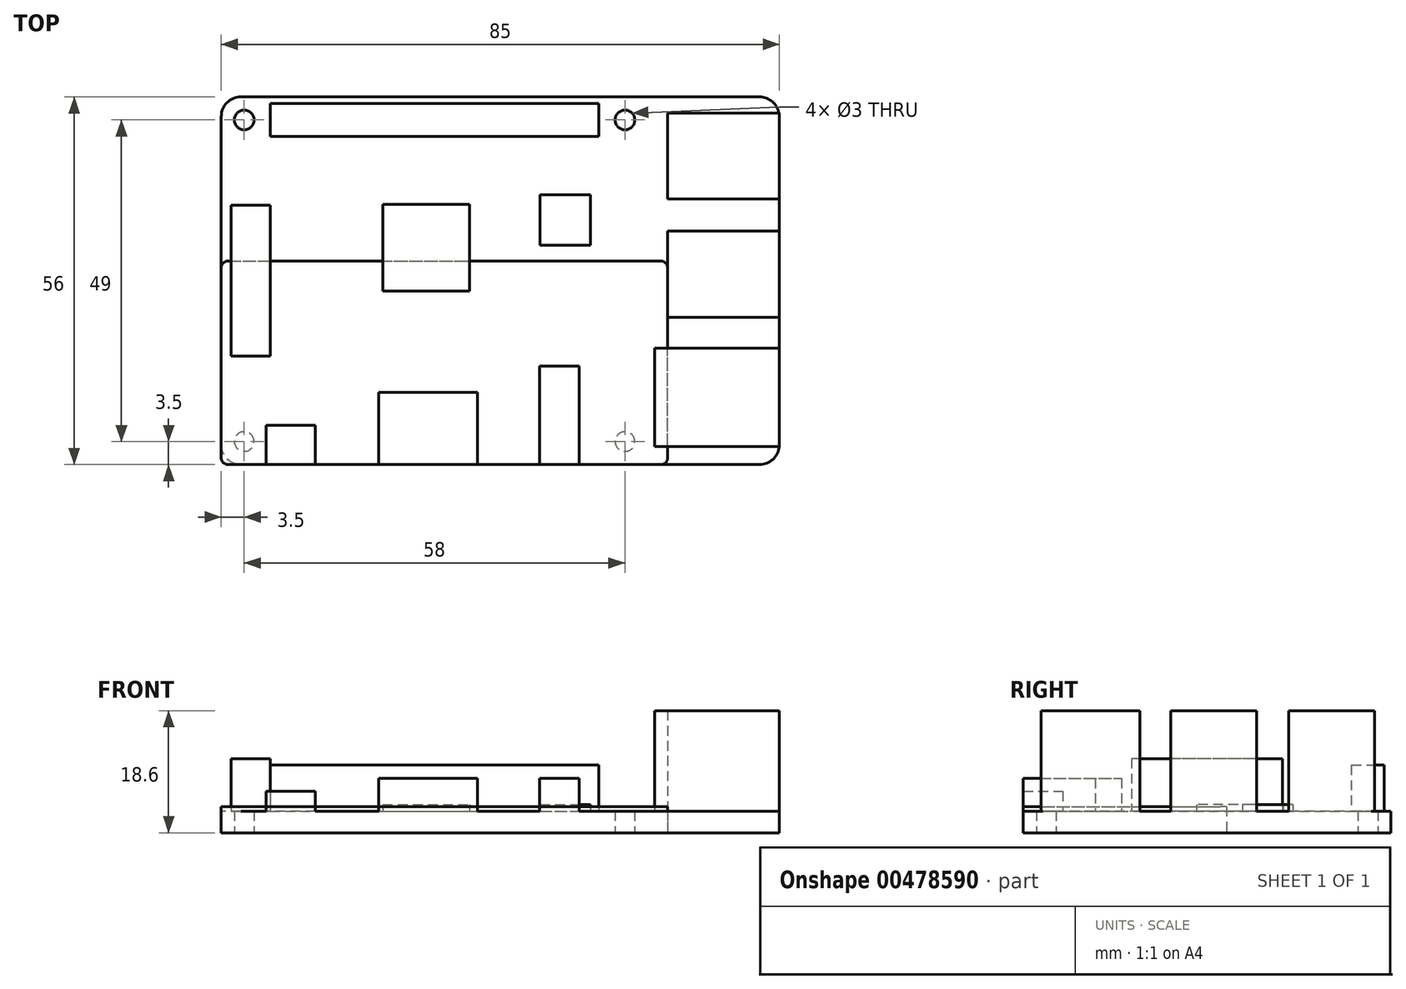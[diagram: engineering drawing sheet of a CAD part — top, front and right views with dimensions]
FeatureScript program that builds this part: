
annotation { "Feature Type Name" : "Feature", "Feature Type Description" : "" }
export const myFeature = defineFeature(function(context is Context, id is Id, definition is map)
    precondition{}
    {
        {
            var Q0;
            Q0=qCreatedBy(makeId("Top.planeOp"),FACE);
            var sketch = newSketch(context, id + "F0", { "sketchPlane" : qUnion([Q0])});
            skLineSegment(sketch, "E0.bottom", {"start": v(0, 0) * mm, "end": v(85, 0) * mm});
            skLineSegment(sketch, "E0.top", {"start": v(0, 56) * mm, "end": v(85, 56) * mm});
            skLineSegment(sketch, "E0.left", {"start": v(0, 0) * mm, "end": v(0, 56) * mm});
            skLineSegment(sketch, "E0.right", {"start": v(85, 0) * mm, "end": v(85, 56) * mm});
            skCircle(sketch, "E1", {"center": v(3.5, 52.5) * mm, "radius": 1.5 * mm});
            skLineSegment(sketch, "E2", {"start": v(0, 28) * mm, "end": v(85, 28) * mm, "construction": true});
            skLineSegment(sketch, "E3", {"start": v(32.5, 56) * mm, "end": v(32.5, 0) * mm, "construction": true});
            skCircle(sketch, "E4.MirrorC", {"center": v(3.5, 3.5) * mm, "radius": 1.5 * mm});
            skCircle(sketch, "E5.MirrorC", {"center": v(61.5, 3.5) * mm, "radius": 1.5 * mm});
            skCircle(sketch, "E6.MirrorC", {"center": v(61.5, 52.5) * mm, "radius": 1.5 * mm});
            skSolve(sketch);
        }
        {
            var Q0;
            Q0=makeQuery(id+"F0.imprint","IMPRINT",FACE,{"disambiguationData":[TD([[makeQuery(id+"F0.imprint","IMPRINT",EDGE,{"derivedFrom":sQuery(id+"F0.wireOp",EDGE,"E0.bottom")}),1.0]])]});
            extrude(context, id + "F1", {"entities" : qUnion([Q0]), "depth" : 3.3 * mm});
        }
        {
            var Q0;
            Q0=makeQuery(id+"F1.opExtrude","SWEPT_EDGE",EDGE,{"disambiguationData":[OSD([sQuery(id+"F0.wireOp",EDGE,"E0.top"),sQuery(id+"F0.wireOp",EDGE,"E0.left")])]});
            var Q1;
            Q1=makeQuery(id+"F1.opExtrude","SWEPT_EDGE",EDGE,{"disambiguationData":[OSD([sQuery(id+"F0.wireOp",EDGE,"E0.top"),sQuery(id+"F0.wireOp",EDGE,"E0.right")])]});
            var Q2;
            Q2=makeQuery(id+"F1.opExtrude","SWEPT_EDGE",EDGE,{"disambiguationData":[OSD([sQuery(id+"F0.wireOp",EDGE,"E0.bottom"),sQuery(id+"F0.wireOp",EDGE,"E0.left")])]});
            var Q3;
            Q3=makeQuery(id+"F1.opExtrude","SWEPT_EDGE",EDGE,{"disambiguationData":[OSD([sQuery(id+"F0.wireOp",EDGE,"E0.bottom"),sQuery(id+"F0.wireOp",EDGE,"E0.right")])]});
            fillet(context, id + "F2", {"entities" : qUnion([Q0, Q1, Q2, Q3]), "radius" : 3 * mm, "tangentPropagation" : true, "allowEdgeOverflow" : false});
        }
        {
            var Q0;
            Q0=makeQuery(id+"F1.opExtrude","CAP_FACE",FACE,{"disambiguationData":[OSD([sQuery(id+"F0.wireOp",EDGE,"E0.bottom"),sQuery(id+"F0.wireOp",EDGE,"E0.top"),sQuery(id+"F0.wireOp",EDGE,"E0.left"),sQuery(id+"F0.wireOp",EDGE,"E0.right"),sQuery(id+"F0.wireOp",EDGE,"E1"),sQuery(id+"F0.wireOp",EDGE,"E4.MirrorC"),sQuery(id+"F0.wireOp",EDGE,"E5.MirrorC"),sQuery(id+"F0.wireOp",EDGE,"E6.MirrorC")])],"isStart":false});
            var sketch = newSketch(context, id + "F3", { "sketchPlane" : qUnion([Q0])});
            skLineSegment(sketch, "E7.bottom", {"start": v(7.5, 50) * mm, "end": v(57.5, 50) * mm});
            skLineSegment(sketch, "E7.top", {"start": v(7.5, 55) * mm, "end": v(57.5, 55) * mm});
            skLineSegment(sketch, "E7.left", {"start": v(7.5, 50) * mm, "end": v(7.5, 55) * mm});
            skLineSegment(sketch, "E7.right", {"start": v(57.5, 50) * mm, "end": v(57.5, 55) * mm});
            skCircle(sketch, "E8.0", {"center": v(3.5, 52.5) * mm, "radius": 1.5 * mm, "construction": true});
            skLineSegment(sketch, "E9", {"start": v(32.5, 55) * mm, "end": v(32.5, 50) * mm, "construction": true});
            skLineSegment(sketch, "E10", {"start": v(3.5, 52.5) * mm, "end": v(32.5, 52.5) * mm, "construction": true});
            skSolve(sketch);
        }
        {
            var Q0;
            Q0 = qSketchRegion(id + "F3", true);
            extrude(context, id + "F4", {"entities" : qUnion([Q0]), "operationType" : NewBodyOperationType.ADD, "depth" : 7 * mm});
        }
        {
            var Q0;
            Q0=makeQuery(id+"F1.opExtrude","CAP_FACE",FACE,{"disambiguationData":[OSD([sQuery(id+"F0.wireOp",EDGE,"E0.bottom"),sQuery(id+"F0.wireOp",EDGE,"E0.top"),sQuery(id+"F0.wireOp",EDGE,"E0.left"),sQuery(id+"F0.wireOp",EDGE,"E0.right"),sQuery(id+"F0.wireOp",EDGE,"E1"),sQuery(id+"F0.wireOp",EDGE,"E4.MirrorC"),sQuery(id+"F0.wireOp",EDGE,"E5.MirrorC"),sQuery(id+"F0.wireOp",EDGE,"E6.MirrorC")])],"isStart":false});
            var sketch = newSketch(context, id + "F5", { "sketchPlane" : qUnion([Q0])});
            skLineSegment(sketch, "E11.bottom", {"start": v(1.5, 39.5) * mm, "end": v(7.5, 39.5) * mm});
            skLineSegment(sketch, "E11.top", {"start": v(1.5, 16.5) * mm, "end": v(7.5, 16.5) * mm});
            skLineSegment(sketch, "E11.left", {"start": v(1.5, 39.5) * mm, "end": v(1.5, 16.5) * mm});
            skLineSegment(sketch, "E11.right", {"start": v(7.5, 39.5) * mm, "end": v(7.5, 16.5) * mm});
            skCircle(sketch, "E12.0", {"center": v(3.5, 52.5) * mm, "radius": 1.5 * mm, "construction": true});
            skCircle(sketch, "E13.0", {"center": v(3.5, 3.5) * mm, "radius": 1.5 * mm, "construction": true});
            skLineSegment(sketch, "E14", {"start": v(3.5, 3.5) * mm, "end": v(3.5, 52.5) * mm, "construction": true});
            skLineSegment(sketch, "E15", {"start": v(3.5, 28) * mm, "end": v(7.5, 28) * mm, "construction": true});
            skSolve(sketch);
        }
        {
            var Q0;
            Q0 = qSketchRegion(id + "F5", true);
            extrude(context, id + "F6", {"entities" : qUnion([Q0]), "operationType" : NewBodyOperationType.ADD, "depth" : 8 * mm});
        }
        {
            var Q0;
            Q0=makeQuery(id+"F1.opExtrude","CAP_FACE",FACE,{"disambiguationData":[OSD([sQuery(id+"F0.wireOp",EDGE,"E0.bottom"),sQuery(id+"F0.wireOp",EDGE,"E0.top"),sQuery(id+"F0.wireOp",EDGE,"E0.left"),sQuery(id+"F0.wireOp",EDGE,"E0.right"),sQuery(id+"F0.wireOp",EDGE,"E1"),sQuery(id+"F0.wireOp",EDGE,"E4.MirrorC"),sQuery(id+"F0.wireOp",EDGE,"E5.MirrorC"),sQuery(id+"F0.wireOp",EDGE,"E6.MirrorC")])],"isStart":false});
            var sketch = newSketch(context, id + "F7", { "sketchPlane" : qUnion([Q0])});
            skLineSegment(sketch, "E16.bottom", {"start": v(68, 53.55) * mm, "end": v(85, 53.55) * mm});
            skLineSegment(sketch, "E16.top", {"start": v(68, 40.45) * mm, "end": v(85, 40.45) * mm});
            skLineSegment(sketch, "E16.left", {"start": v(68, 53.55) * mm, "end": v(68, 40.45) * mm});
            skLineSegment(sketch, "E16.right", {"start": v(85, 53.55) * mm, "end": v(85, 40.45) * mm});
            skLineSegment(sketch, "E17.bottom", {"start": v(68, 35.55) * mm, "end": v(85, 35.55) * mm});
            skLineSegment(sketch, "E17.top", {"start": v(68, 22.45) * mm, "end": v(85, 22.45) * mm});
            skLineSegment(sketch, "E17.left", {"start": v(68, 35.55) * mm, "end": v(68, 22.45) * mm});
            skLineSegment(sketch, "E17.right", {"start": v(85, 35.55) * mm, "end": v(85, 22.45) * mm});
            skLineSegment(sketch, "E18.bottom", {"start": v(66, 17.75) * mm, "end": v(85, 17.75) * mm});
            skLineSegment(sketch, "E18.top", {"start": v(66, 2.75) * mm, "end": v(85, 2.75) * mm});
            skLineSegment(sketch, "E18.left", {"start": v(66, 17.75) * mm, "end": v(66, 2.75) * mm});
            skLineSegment(sketch, "E18.right", {"start": v(85, 17.75) * mm, "end": v(85, 2.75) * mm});
            skLineSegment(sketch, "E19", {"start": v(68, 29) * mm, "end": v(85, 29) * mm, "construction": true});
            skLineSegment(sketch, "E20", {"start": v(68, 47) * mm, "end": v(85, 47) * mm, "construction": true});
            skLineSegment(sketch, "E21", {"start": v(66, 10.25) * mm, "end": v(85, 10.25) * mm, "construction": true});
            skSolve(sketch);
        }
        {
            var Q0;
            Q0 = qSketchRegion(id + "F7", true);
            extrude(context, id + "F8", {"entities" : qUnion([Q0]), "operationType" : NewBodyOperationType.ADD, "depth" : 15.3 * mm});
        }
        {
            var Q0;
            Q0=makeQuery(id+"F1.opExtrude","CAP_FACE",FACE,{"disambiguationData":[OSD([sQuery(id+"F0.wireOp",EDGE,"E0.bottom"),sQuery(id+"F0.wireOp",EDGE,"E0.top"),sQuery(id+"F0.wireOp",EDGE,"E0.left"),sQuery(id+"F0.wireOp",EDGE,"E0.right"),sQuery(id+"F0.wireOp",EDGE,"E1"),sQuery(id+"F0.wireOp",EDGE,"E4.MirrorC"),sQuery(id+"F0.wireOp",EDGE,"E5.MirrorC"),sQuery(id+"F0.wireOp",EDGE,"E6.MirrorC")])],"isStart":false});
            var sketch = newSketch(context, id + "F9", { "sketchPlane" : qUnion([Q0])});
            skLineSegment(sketch, "E22.bottom", {"start": v(24, 0) * mm, "end": v(39, 0) * mm});
            skLineSegment(sketch, "E22.top", {"start": v(24, 11) * mm, "end": v(39, 11) * mm});
            skLineSegment(sketch, "E22.left", {"start": v(24, 0) * mm, "end": v(24, 11) * mm});
            skLineSegment(sketch, "E22.right", {"start": v(39, 0) * mm, "end": v(39, 11) * mm});
            skLineSegment(sketch, "E23", {"start": v(31.5, 11) * mm, "end": v(31.5, 0) * mm, "construction": true});
            skSolve(sketch);
        }
        {
            var Q0;
            Q0 = qSketchRegion(id + "F9", true);
            extrude(context, id + "F10", {"entities" : qUnion([Q0]), "operationType" : NewBodyOperationType.ADD, "depth" : 5 * mm});
        }
        {
            var Q0;
            Q0=makeQuery(id+"F1.opExtrude","CAP_FACE",FACE,{"disambiguationData":[OSD([sQuery(id+"F0.wireOp",EDGE,"E0.bottom"),sQuery(id+"F0.wireOp",EDGE,"E0.top"),sQuery(id+"F0.wireOp",EDGE,"E0.left"),sQuery(id+"F0.wireOp",EDGE,"E0.right"),sQuery(id+"F0.wireOp",EDGE,"E1"),sQuery(id+"F0.wireOp",EDGE,"E4.MirrorC"),sQuery(id+"F0.wireOp",EDGE,"E5.MirrorC"),sQuery(id+"F0.wireOp",EDGE,"E6.MirrorC")])],"isStart":false});
            var sketch = newSketch(context, id + "F11", { "sketchPlane" : qUnion([Q0])});
            skLineSegment(sketch, "E24.bottom", {"start": v(14.35, 0) * mm, "end": v(6.85, 0) * mm});
            skLineSegment(sketch, "E24.top", {"start": v(14.35, 6) * mm, "end": v(6.85, 6) * mm});
            skLineSegment(sketch, "E24.left", {"start": v(14.35, 0) * mm, "end": v(14.35, 6) * mm});
            skLineSegment(sketch, "E24.right", {"start": v(6.85, 0) * mm, "end": v(6.85, 6) * mm});
            skLineSegment(sketch, "E25", {"start": v(10.6, 6) * mm, "end": v(10.6, 0) * mm, "construction": true});
            skSolve(sketch);
        }
        {
            var Q0;
            Q0 = qSketchRegion(id + "F11", true);
            extrude(context, id + "F12", {"entities" : qUnion([Q0]), "operationType" : NewBodyOperationType.ADD, "depth" : 3 * mm});
        }
        {
            var Q0;
            Q0=makeQuery(id+"F1.opExtrude","CAP_FACE",FACE,{"disambiguationData":[OSD([sQuery(id+"F0.wireOp",EDGE,"E0.bottom"),sQuery(id+"F0.wireOp",EDGE,"E0.top"),sQuery(id+"F0.wireOp",EDGE,"E0.left"),sQuery(id+"F0.wireOp",EDGE,"E0.right"),sQuery(id+"F0.wireOp",EDGE,"E1"),sQuery(id+"F0.wireOp",EDGE,"E4.MirrorC"),sQuery(id+"F0.wireOp",EDGE,"E5.MirrorC"),sQuery(id+"F0.wireOp",EDGE,"E6.MirrorC")])],"isStart":false});
            var sketch = newSketch(context, id + "F13", { "sketchPlane" : qUnion([Q0])});
            skLineSegment(sketch, "E26.bottom", {"start": v(48.5, 0) * mm, "end": v(54.5, 0) * mm});
            skLineSegment(sketch, "E26.top", {"start": v(48.5, 15) * mm, "end": v(54.5, 15) * mm});
            skLineSegment(sketch, "E26.left", {"start": v(48.5, 0) * mm, "end": v(48.5, 15) * mm});
            skLineSegment(sketch, "E26.right", {"start": v(54.5, 0) * mm, "end": v(54.5, 15) * mm});
            skLineSegment(sketch, "E27", {"start": v(51.5, 15) * mm, "end": v(51.5, 0) * mm, "construction": true});
            skSolve(sketch);
        }
        {
            var Q0;
            Q0 = qSketchRegion(id + "F13", true);
            extrude(context, id + "F14", {"entities" : qUnion([Q0]), "operationType" : NewBodyOperationType.ADD, "depth" : 5 * mm});
        }
        {
            var Q0;
            Q0=makeQuery(id+"F1.opExtrude","CAP_FACE",FACE,{"disambiguationData":[OSD([sQuery(id+"F0.wireOp",EDGE,"E0.bottom"),sQuery(id+"F0.wireOp",EDGE,"E0.top"),sQuery(id+"F0.wireOp",EDGE,"E0.left"),sQuery(id+"F0.wireOp",EDGE,"E0.right"),sQuery(id+"F0.wireOp",EDGE,"E1"),sQuery(id+"F0.wireOp",EDGE,"E4.MirrorC"),sQuery(id+"F0.wireOp",EDGE,"E5.MirrorC"),sQuery(id+"F0.wireOp",EDGE,"E6.MirrorC")])],"isStart":false});
            var sketch = newSketch(context, id + "F15", { "sketchPlane" : qUnion([Q0])});
            skLineSegment(sketch, "E28.bottom", {"start": v(24.6, 39.63) * mm, "end": v(37.8, 39.63) * mm});
            skLineSegment(sketch, "E28.top", {"start": v(24.6, 26.43) * mm, "end": v(37.8, 26.43) * mm});
            skLineSegment(sketch, "E28.left", {"start": v(24.6, 39.63) * mm, "end": v(24.6, 26.43) * mm});
            skLineSegment(sketch, "E28.right", {"start": v(37.8, 39.63) * mm, "end": v(37.8, 26.43) * mm});
            skLineSegment(sketch, "E29.bottom", {"start": v(48.57, 41.09) * mm, "end": v(56.24, 41.09) * mm});
            skLineSegment(sketch, "E29.top", {"start": v(48.57, 33.41) * mm, "end": v(56.24, 33.41) * mm});
            skLineSegment(sketch, "E29.left", {"start": v(48.57, 41.09) * mm, "end": v(48.57, 33.41) * mm});
            skLineSegment(sketch, "E29.right", {"start": v(56.24, 41.09) * mm, "end": v(56.24, 33.41) * mm});
            skSolve(sketch);
        }
        {
            var Q0;
            Q0 = qSketchRegion(id + "F15", true);
            extrude(context, id + "F16", {"entities" : qUnion([Q0]), "operationType" : NewBodyOperationType.ADD, "depth" : 1 * mm});
        }
        {
            var Q0;
            Q0=qCreatedBy(makeId("Top.planeOp"),FACE);
            var sketch = newSketch(context, id + "F17", { "sketchPlane" : qUnion([Q0])});
            skLineSegment(sketch, "E30.bottom", {"start": v(0, 0) * mm, "end": v(68, 0) * mm});
            skLineSegment(sketch, "E30.top", {"start": v(0, 31) * mm, "end": v(68, 31) * mm});
            skLineSegment(sketch, "E30.left", {"start": v(0, 0) * mm, "end": v(0, 31) * mm});
            skLineSegment(sketch, "E30.right", {"start": v(68, 0) * mm, "end": v(68, 31) * mm});
            skSolve(sketch);
        }
        {
            var Q0;
            Q0=makeQuery(id+"F17.imprint","IMPRINT",FACE,{"disambiguationData":[TD([[makeQuery(id+"F17.imprint","IMPRINT",EDGE,{"derivedFrom":sQuery(id+"F17.wireOp",EDGE,"E30.bottom")}),1.0]])]});
            extrude(context, id + "F18", {"entities" : qUnion([Q0]), "depth" : 4 * mm, "offsetDistance" : 25 * mm});
        }
        {
            var Q0;
            Q0=makeQuery(id+"F18.opExtrude","SWEPT_EDGE",EDGE,{"disambiguationData":[OSD([sQuery(id+"F17.wireOp",EDGE,"E30.bottom"),sQuery(id+"F17.wireOp",EDGE,"E30.right")])]});
            var Q1;
            Q1=makeQuery(id+"F18.opExtrude","SWEPT_EDGE",EDGE,{"disambiguationData":[OSD([sQuery(id+"F17.wireOp",EDGE,"E30.top"),sQuery(id+"F17.wireOp",EDGE,"E30.right")])]});
            var Q2;
            Q2=makeQuery(id+"F18.opExtrude","SWEPT_EDGE",EDGE,{"disambiguationData":[OSD([sQuery(id+"F17.wireOp",EDGE,"E30.bottom"),sQuery(id+"F17.wireOp",EDGE,"E30.left")])]});
            var Q3;
            Q3=makeQuery(id+"F18.opExtrude","SWEPT_EDGE",EDGE,{"disambiguationData":[OSD([sQuery(id+"F17.wireOp",EDGE,"E30.top"),sQuery(id+"F17.wireOp",EDGE,"E30.left")])]});
            fillet(context, id + "F19", {"entities" : qUnion([Q0, Q1, Q2, Q3]), "radius" : 1 * mm, "tangentPropagation" : true, "allowEdgeOverflow" : false});
        }
    });
